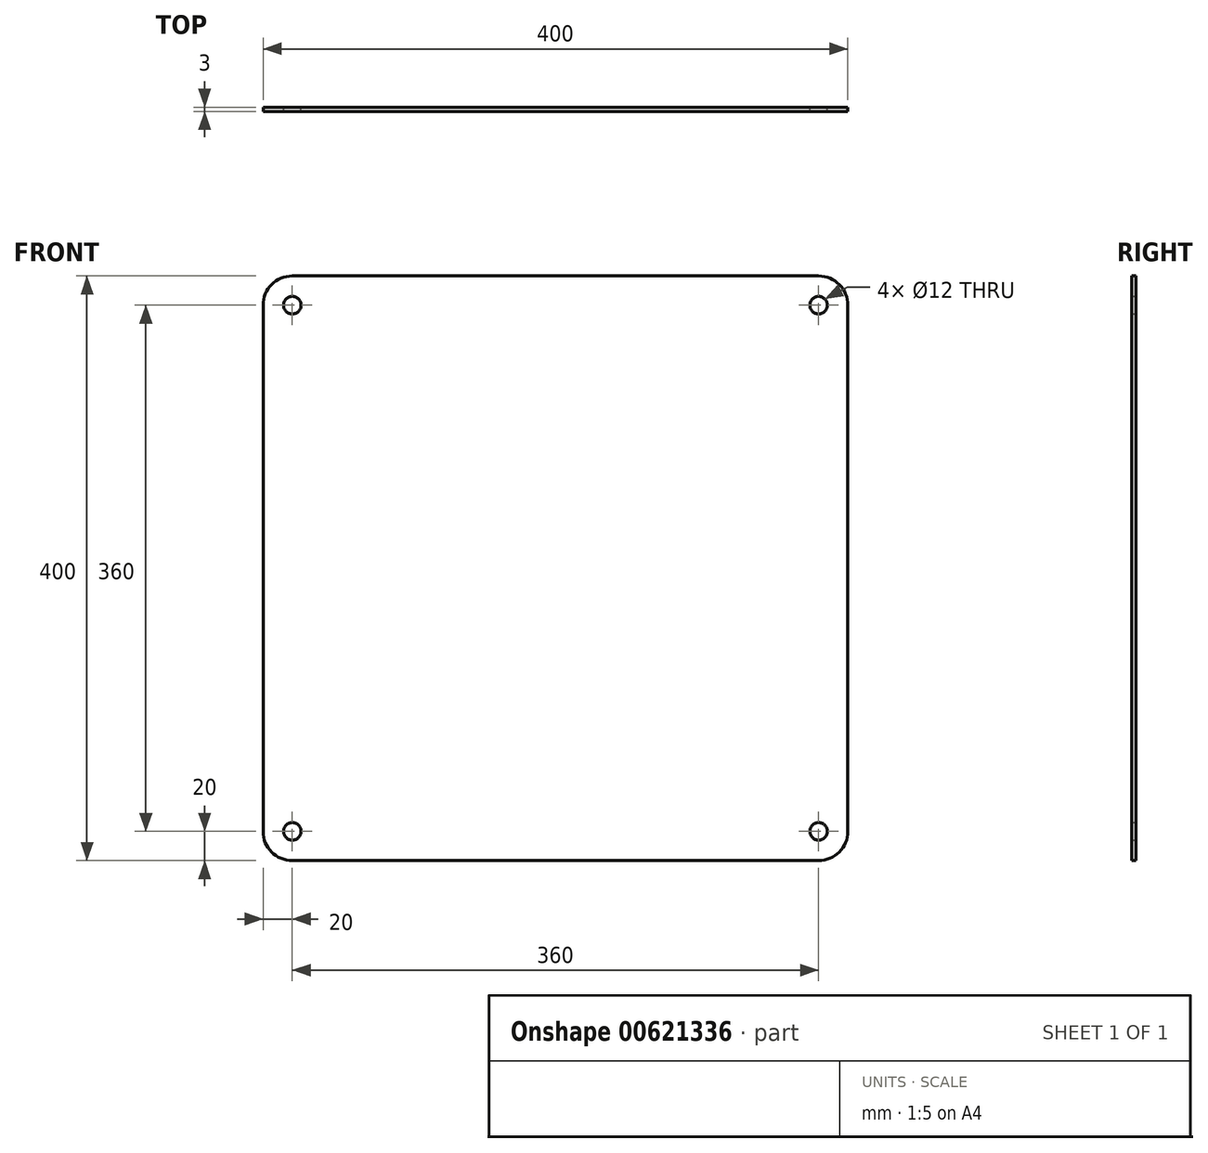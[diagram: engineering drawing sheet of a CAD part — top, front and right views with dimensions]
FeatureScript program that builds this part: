
annotation { "Feature Type Name" : "Feature", "Feature Type Description" : "" }
export const myFeature = defineFeature(function(context is Context, id is Id, definition is map)
    precondition{}
    {
        {
            var Q0;
            Q0=qCreatedBy(makeId("Front.planeOp"),FACE);
            var sketch = newSketch(context, id + "F0", { "sketchPlane" : qUnion([Q0])});
            skLineSegment(sketch, "E0.bottom", {"start": v(180, 200) * mm, "end": v(-180, 200) * mm});
            skLineSegment(sketch, "E0.top", {"start": v(180, -200) * mm, "end": v(-180, -200) * mm});
            skLineSegment(sketch, "E0.left", {"start": v(200, 180) * mm, "end": v(200, -180) * mm});
            skLineSegment(sketch, "E0.right", {"start": v(-200, 180) * mm, "end": v(-200, -180) * mm});
            skPoint(sketch, "E0.middle", {"position": v(0, 0) * mm});
            skPoint(sketch, "E1.visualSharp", {"position": v(-200, 200) * mm});
            skArc(sketch, "E1.filletArc", {"start": v(-180, 200) * mm, "mid": v(-194.14, 194.14) * mm, "end": v(-200, 180) * mm});
            skPoint(sketch, "E2.visualSharp", {"position": v(200, 200) * mm});
            skArc(sketch, "E2.filletArc", {"start": v(200, 180) * mm, "mid": v(194.14, 194.14) * mm, "end": v(180, 200) * mm});
            skPoint(sketch, "E3.visualSharp", {"position": v(200, -200) * mm});
            skArc(sketch, "E3.filletArc", {"start": v(180, -200) * mm, "mid": v(194.14, -194.14) * mm, "end": v(200, -180) * mm});
            skPoint(sketch, "E4.visualSharp", {"position": v(-200, -200) * mm});
            skArc(sketch, "E4.filletArc", {"start": v(-200, -180) * mm, "mid": v(-194.14, -194.14) * mm, "end": v(-180, -200) * mm});
            skCircle(sketch, "E5", {"center": v(-180, -180) * mm, "radius": 6 * mm});
            skCircle(sketch, "E6.MirrorC", {"center": v(180, -180) * mm, "radius": 6 * mm});
            skCircle(sketch, "E7.MirrorC", {"center": v(-180, 180) * mm, "radius": 6 * mm});
            skCircle(sketch, "E8.MirrorC", {"center": v(180, 180) * mm, "radius": 6 * mm});
            skSolve(sketch);
        }
        {
            var Q0;
            Q0=makeQuery(id+"F0.imprint","IMPRINT",FACE,{"disambiguationData":[TD([[makeQuery(id+"F0.imprint","IMPRINT",EDGE,{"derivedFrom":sQuery(id+"F0.wireOp",EDGE,"E0.bottom")}),1.0]])]});
            extrude(context, id + "F1", {"entities" : qUnion([Q0]), "depth" : 3 * mm, "offsetDistance" : 25 * mm});
        }
    });
